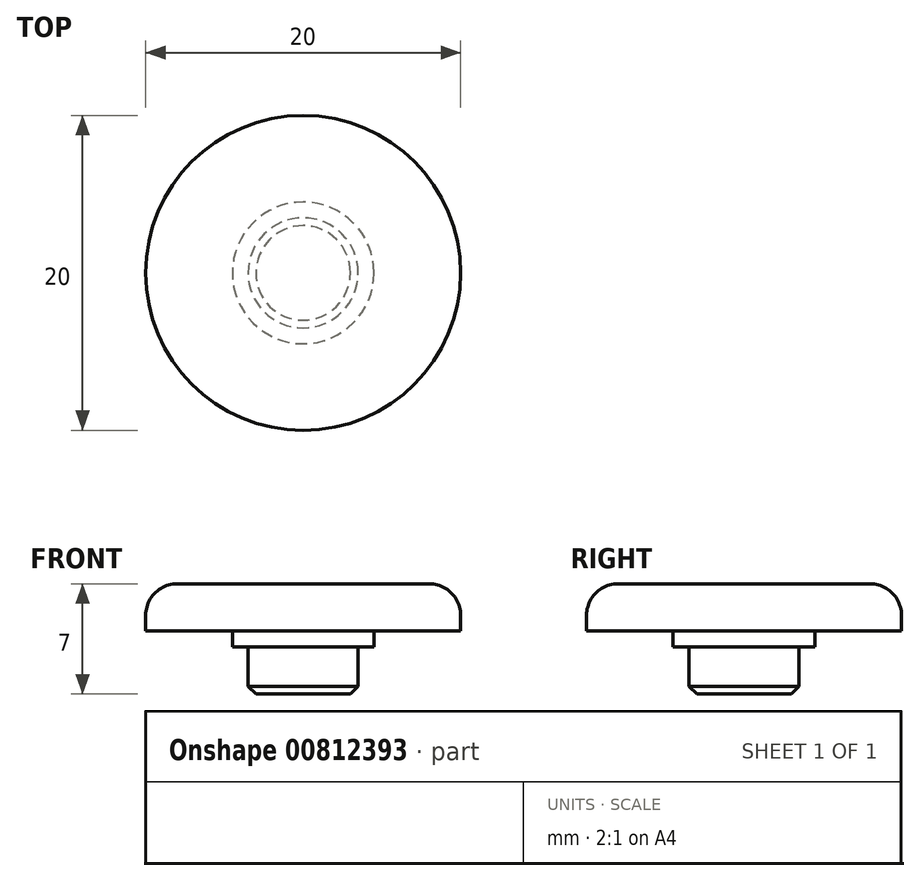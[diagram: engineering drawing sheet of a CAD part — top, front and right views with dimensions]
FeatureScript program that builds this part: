
annotation { "Feature Type Name" : "Feature", "Feature Type Description" : "" }
export const myFeature = defineFeature(function(context is Context, id is Id, definition is map)
    precondition{}
    {
        {
            var Q0;
            Q0=qCreatedBy(makeId("Top.planeOp"),FACE);
            var sketch = newSketch(context, id + "F0", { "sketchPlane" : qUnion([Q0])});
            skCircle(sketch, "E0", {"center": v(0, 0) * mm, "radius": 10 * mm});
            skCircle(sketch, "E1", {"center": v(0, 0) * mm, "radius": 4.5 * mm});
            skCircle(sketch, "E2", {"center": v(0, 0) * mm, "radius": 3.5 * mm});
            skSolve(sketch);
        }
        {
            var Q0;
            Q0=makeQuery(id+"F0.imprint","IMPRINT",FACE,{"disambiguationData":[TD([[makeQuery(id+"F0.imprint","IMPRINT",EDGE,{"derivedFrom":sQuery(id+"F0.wireOp",EDGE,"E2")}),1.0]])]});
            extrude(context, id + "F1", {"entities" : qUnion([Q0]), "oppositeDirection" : true, "depth" : 7 * mm, "offsetDistance" : 25 * mm});
        }
        {
            var Q0;
            Q0=makeQuery(id+"F0.imprint","IMPRINT",FACE,{"disambiguationData":[TD([[makeQuery(id+"F0.imprint","IMPRINT",EDGE,{"derivedFrom":sQuery(id+"F0.wireOp",EDGE,"E1")}),1.0]])]});
            extrude(context, id + "F2", {"entities" : qUnion([Q0]), "operationType" : NewBodyOperationType.ADD, "oppositeDirection" : true, "depth" : 4 * mm, "offsetDistance" : 25 * mm});
        }
        {
            var Q0;
            Q0=makeQuery(id+"F0.imprint","IMPRINT",FACE,{"disambiguationData":[TD([[makeQuery(id+"F0.imprint","IMPRINT",EDGE,{"derivedFrom":sQuery(id+"F0.wireOp",EDGE,"E0")}),1.0]])]});
            extrude(context, id + "F3", {"entities" : qUnion([Q0]), "operationType" : NewBodyOperationType.ADD, "oppositeDirection" : true, "depth" : 3 * mm, "offsetDistance" : 25 * mm});
        }
        {
            var Q0;
            Q0=makeQuery(id+"F3.opExtrude","CAP_EDGE",EDGE,{"disambiguationData":[OSD([sQuery(id+"F0.wireOp",EDGE,"E0")])],"isStart":true});
            fillet(context, id + "F4", {"entities" : qUnion([Q0]), "radius" : 2 * mm, "tangentPropagation" : true, "allowEdgeOverflow" : false});
        }
        {
            var Q0;
            Q0=makeQuery(id+"F1.opExtrude","CAP_EDGE",EDGE,{"disambiguationData":[OSD([sQuery(id+"F0.wireOp",EDGE,"E2")])],"isStart":false});
            chamfer(context, id + "F5", {"entities" : qUnion([Q0]), "width" : 0.5 * mm, "tangentPropagation" : true});
        }
    });
